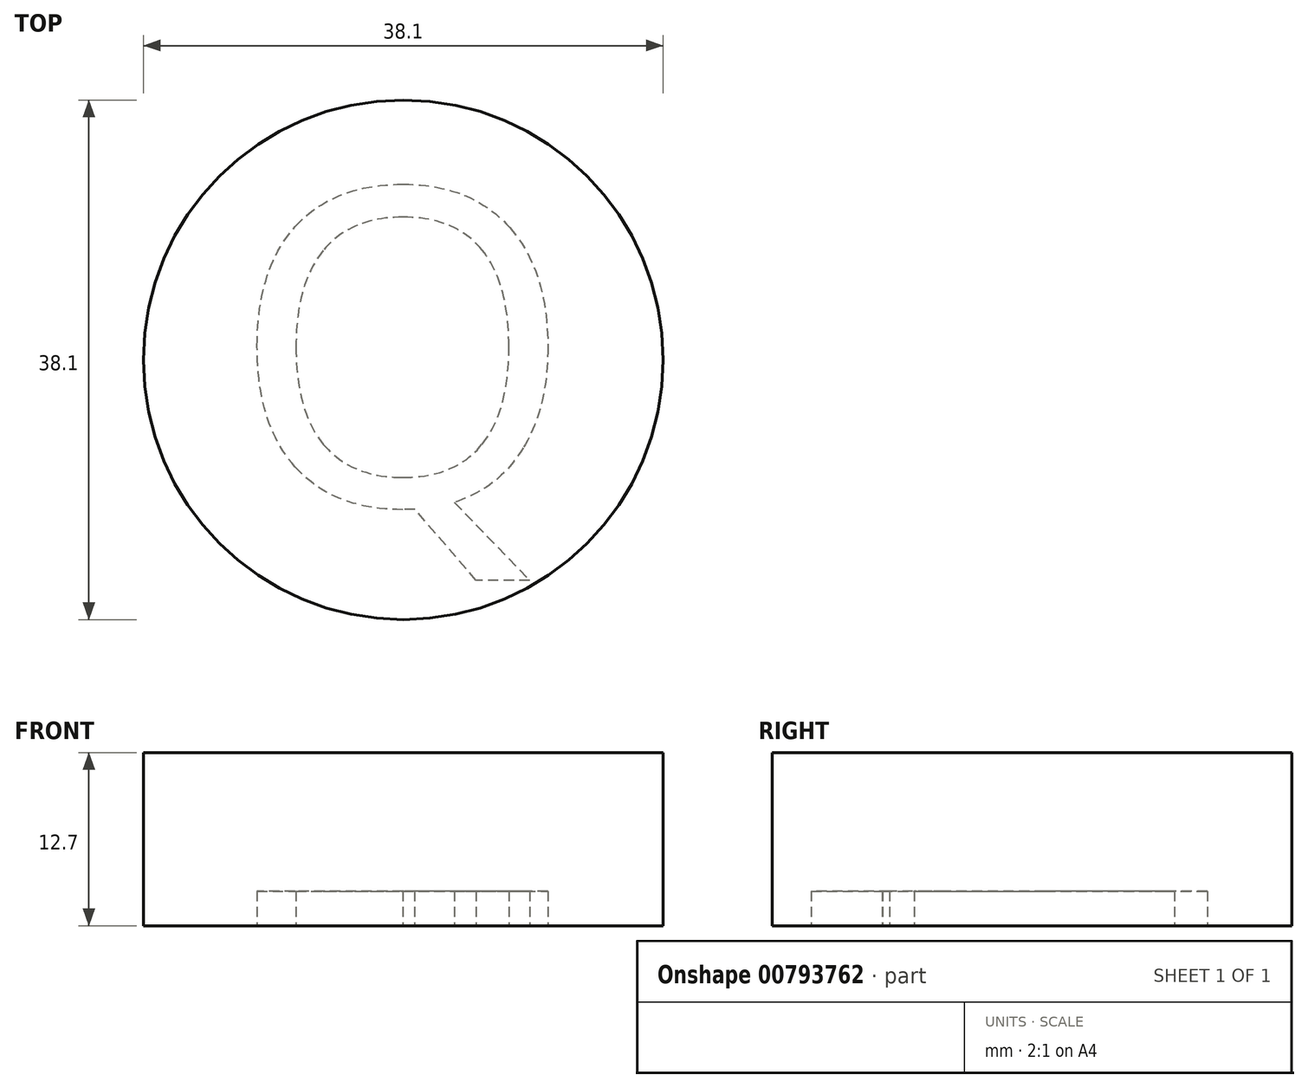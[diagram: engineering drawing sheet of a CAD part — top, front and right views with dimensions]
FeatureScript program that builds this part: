
annotation { "Feature Type Name" : "Feature", "Feature Type Description" : "" }
export const myFeature = defineFeature(function(context is Context, id is Id, definition is map)
    precondition{}
    {
        {
            var Q0;
            Q0=qCreatedBy(makeId("Top.planeOp"),FACE);
            var sketch = newSketch(context, id + "F0", { "sketchPlane" : qUnion([Q0])});
            skCircle(sketch, "E0", {"center": v(0, 0) * mm, "radius": 19.05 * mm});
            skSolve(sketch);
        }
        {
            var Q0;
            Q0=makeQuery(id+"F0.imprint","IMPRINT",FACE,{"disambiguationData":[TD([[makeQuery(id+"F0.imprint","IMPRINT",EDGE,{"derivedFrom":sQuery(id+"F0.wireOp",EDGE,"E0")}),1.0]])]});
            extrude(context, id + "F1", {"entities" : qUnion([Q0]), "depth" : 12.7 * mm, "offsetDistance" : 25.4 * mm});
        }
        {
            var Q0;
            Q0=qCreatedBy(makeId("Top.planeOp"),FACE);
            var sketch = newSketch(context, id + "F2", { "sketchPlane" : qUnion([Q0])});
            skText(sketch, "E1", { "text": "Q", "fontName": "OpenSans-Regular.ttf"});
            const initialGuessF2  = {"E1": [-0.0127, -0.01067, 1, 0, 0.02337]};
            skSetInitialGuess(sketch, initialGuessF2);
            skSolve(sketch);
        }
        {
            var Q0;
            Q0 = qSketchRegion(id + "F2", true);
            extrude(context, id + "F3", {"entities" : qUnion([Q0]), "operationType" : NewBodyOperationType.REMOVE, "depth" : 2.54 * mm, "offsetDistance" : 25.4 * mm});
        }
    });
